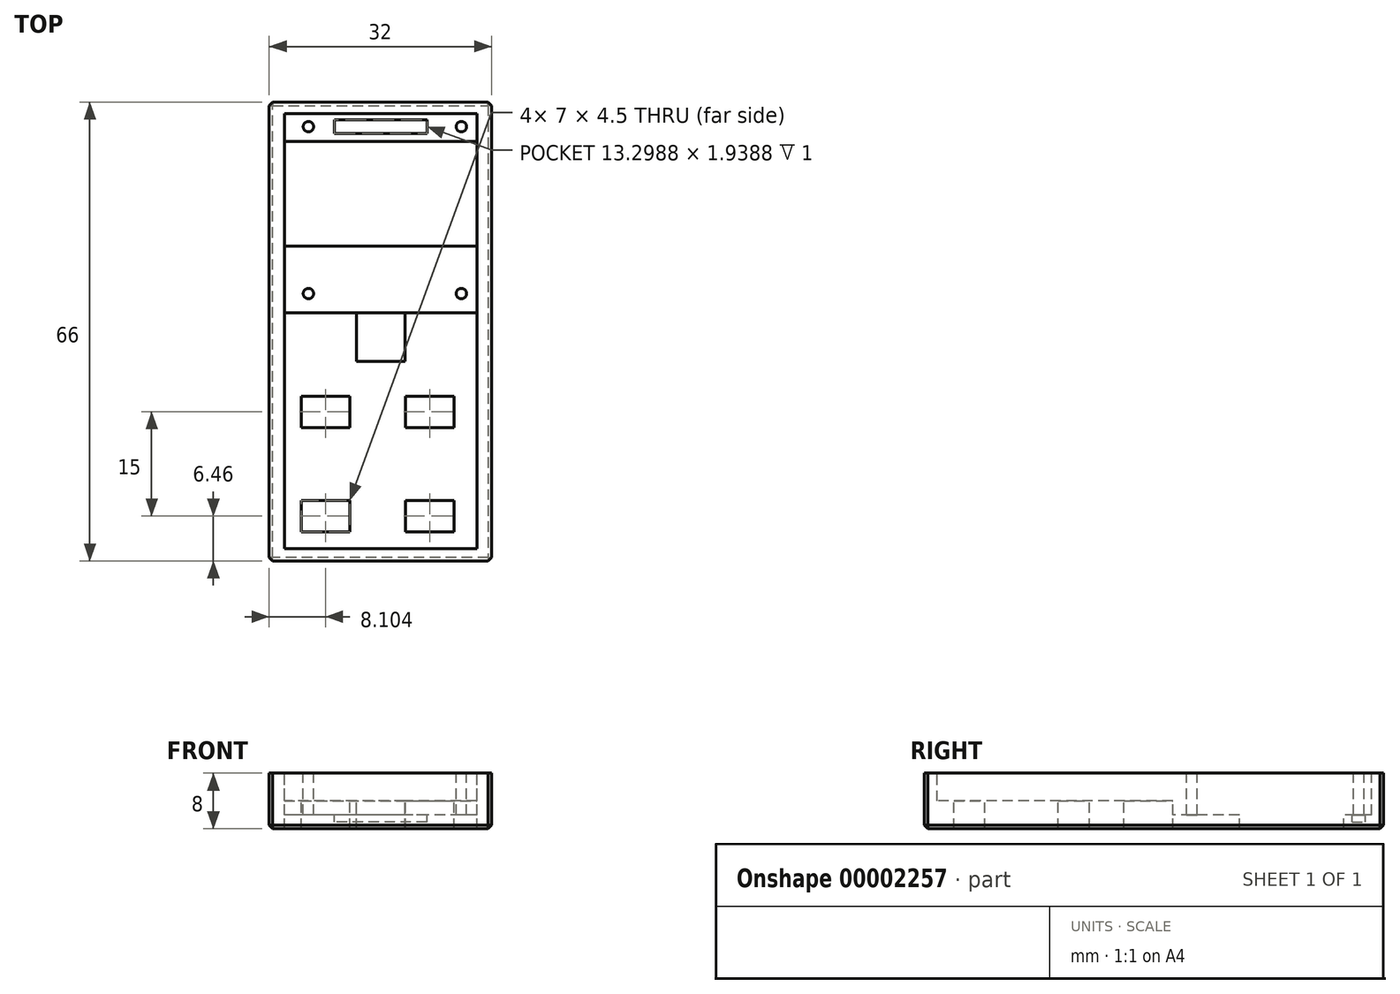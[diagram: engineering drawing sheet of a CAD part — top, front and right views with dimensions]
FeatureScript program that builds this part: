
annotation { "Feature Type Name" : "Feature", "Feature Type Description" : "" }
export const myFeature = defineFeature(function(context is Context, id is Id, definition is map)
    precondition{}
    {
        {
            var Q0;
            Q0=qCreatedBy(makeId("Top.planeOp"),FACE);
            var sketch = newSketch(context, id + "F0", { "sketchPlane" : qUnion([Q0])});
            skLineSegment(sketch, "E0.bottom", {"start": v(-16.74, 44.5) * mm, "end": v(15.26, 44.5) * mm});
            skLineSegment(sketch, "E0.top", {"start": v(-16.74, -21.5) * mm, "end": v(15.26, -21.5) * mm});
            skLineSegment(sketch, "E0.left", {"start": v(-16.74, 44.5) * mm, "end": v(-16.74, -21.5) * mm});
            skLineSegment(sketch, "E0.right", {"start": v(15.26, 44.5) * mm, "end": v(15.26, -21.5) * mm});
            skSolve(sketch);
        }
        {
            var Q0;
            Q0=makeQuery(id+"F0.imprint","IMPRINT",FACE,{"disambiguationData":[TD([[makeQuery(id+"F0.imprint","IMPRINT",EDGE,{"derivedFrom":sQuery(id+"F0.wireOp",EDGE,"E0.bottom")}),-1.0]])]});
            extrude(context, id + "F1", {"entities" : qUnion([Q0]), "depth" : 8 * mm});
        }
        {
            var Q0;
            Q0=makeQuery(id+"F1.opExtrude","CAP_FACE",FACE,{"disambiguationData":[OSD([sQuery(id+"F0.wireOp",EDGE,"E0.bottom"),sQuery(id+"F0.wireOp",EDGE,"E0.top"),sQuery(id+"F0.wireOp",EDGE,"E0.left"),sQuery(id+"F0.wireOp",EDGE,"E0.right")])],"isStart":false});
            var sketch = newSketch(context, id + "F2", { "sketchPlane" : qUnion([Q0])});
            skLineSegment(sketch, "E1.bottom", {"start": v(-14.54, 42.81) * mm, "end": v(13.16, 42.81) * mm});
            skLineSegment(sketch, "E1.top", {"start": v(-14.54, -19.69) * mm, "end": v(13.16, -19.69) * mm});
            skLineSegment(sketch, "E1.left", {"start": v(-14.54, 42.81) * mm, "end": v(-14.54, -19.69) * mm});
            skLineSegment(sketch, "E1.right", {"start": v(13.16, 42.81) * mm, "end": v(13.16, -19.69) * mm});
            skLineSegment(sketch, "E2.bottom", {"start": v(13.16, 38.81) * mm, "end": v(-14.54, 38.81) * mm});
            skLineSegment(sketch, "E2.top", {"start": v(13.16, 23.81) * mm, "end": v(-14.54, 23.81) * mm});
            skLineSegment(sketch, "E2.left", {"start": v(13.16, 38.81) * mm, "end": v(13.16, 23.81) * mm});
            skLineSegment(sketch, "E2.right", {"start": v(-14.54, 38.81) * mm, "end": v(-14.54, 23.81) * mm});
            skCircle(sketch, "E3", {"center": v(10.91, 40.96) * mm, "radius": 0.75 * mm});
            skCircle(sketch, "E4.1.0.0", {"center": v(-11.09, 40.96) * mm, "radius": 0.75 * mm});
            skLineSegment(sketch, "E4.direction1", {"start": v(10.91, 40.96) * mm, "end": v(-11.09, 40.96) * mm, "construction": true});
            skCircle(sketch, "E5.0.1.0", {"center": v(-11.09, 16.96) * mm, "radius": 0.75 * mm});
            skCircle(sketch, "E5.0.1.1", {"center": v(10.91, 16.96) * mm, "radius": 0.75 * mm});
            skLineSegment(sketch, "E5.direction1", {"start": v(-11.09, 40.96) * mm, "end": v(13.91, 40.96) * mm, "construction": true});
            skLineSegment(sketch, "E5.direction2", {"start": v(-11.09, 40.96) * mm, "end": v(-11.09, 16.96) * mm, "construction": true});
            skLineSegment(sketch, "E6.bottom", {"start": v(-12.14, -17.29) * mm, "end": v(-5.14, -17.29) * mm});
            skLineSegment(sketch, "E6.top", {"start": v(-12.14, -12.79) * mm, "end": v(-5.14, -12.79) * mm});
            skLineSegment(sketch, "E6.left", {"start": v(-12.14, -17.29) * mm, "end": v(-12.14, -12.79) * mm});
            skLineSegment(sketch, "E6.right", {"start": v(-5.14, -17.29) * mm, "end": v(-5.14, -12.79) * mm});
            skLineSegment(sketch, "E7.0.1.0", {"start": v(-12.14, 2.21) * mm, "end": v(-5.14, 2.21) * mm});
            skLineSegment(sketch, "E7.0.1.1", {"start": v(-12.14, -2.29) * mm, "end": v(-12.14, 2.21) * mm});
            skLineSegment(sketch, "E7.0.1.2", {"start": v(-12.14, -2.29) * mm, "end": v(-5.14, -2.29) * mm});
            skLineSegment(sketch, "E7.0.1.3", {"start": v(-5.14, -2.29) * mm, "end": v(-5.14, 2.21) * mm});
            skLineSegment(sketch, "E7.1.0.0", {"start": v(2.86, -12.79) * mm, "end": v(9.86, -12.79) * mm});
            skLineSegment(sketch, "E7.1.0.1", {"start": v(2.86, -17.29) * mm, "end": v(2.86, -12.79) * mm});
            skLineSegment(sketch, "E7.1.0.2", {"start": v(2.86, -17.29) * mm, "end": v(9.86, -17.29) * mm});
            skLineSegment(sketch, "E7.1.0.3", {"start": v(9.86, -17.29) * mm, "end": v(9.86, -12.79) * mm});
            skLineSegment(sketch, "E7.1.1.0", {"start": v(2.86, 2.21) * mm, "end": v(9.86, 2.21) * mm});
            skLineSegment(sketch, "E7.1.1.1", {"start": v(2.86, -2.29) * mm, "end": v(2.86, 2.21) * mm});
            skLineSegment(sketch, "E7.1.1.2", {"start": v(2.86, -2.29) * mm, "end": v(9.86, -2.29) * mm});
            skLineSegment(sketch, "E7.1.1.3", {"start": v(9.86, -2.29) * mm, "end": v(9.86, 2.21) * mm});
            skLineSegment(sketch, "E7.direction1", {"start": v(-12.7, -17.29) * mm, "end": v(2.3, -17.29) * mm, "construction": true});
            skLineSegment(sketch, "E7.direction2", {"start": v(-12.7, -17.29) * mm, "end": v(-12.7, -2.29) * mm, "construction": true});
            skLineSegment(sketch, "E8", {"start": v(-0.69, 42.81) * mm, "end": v(-0.69, 38.81) * mm, "construction": true});
            skLineSegment(sketch, "E9.bottom", {"start": v(5.96, 40) * mm, "end": v(-7.33, 40) * mm});
            skLineSegment(sketch, "E9.top", {"start": v(5.96, 41.93) * mm, "end": v(-7.33, 41.93) * mm});
            skLineSegment(sketch, "E9.left", {"start": v(5.96, 40) * mm, "end": v(5.96, 41.93) * mm});
            skLineSegment(sketch, "E9.right", {"start": v(-7.33, 40) * mm, "end": v(-7.33, 41.93) * mm});
            skPoint(sketch, "E9.middle", {"position": v(-0.69, 40.96) * mm});
            skPoint(sketch, "E9.middle.positionSnap0", {"position": v(-0.69, 40.81) * mm});
            skPoint(sketch, "E9.centerSnap0", {"position": v(-0.69, 40.81) * mm});
            skLineSegment(sketch, "E10", {"start": v(-0.69, 38.81) * mm, "end": v(-0.69, -19.69) * mm, "construction": true});
            skLineSegment(sketch, "E11.bottom", {"start": v(2.81, 7.21) * mm, "end": v(-4.19, 7.21) * mm});
            skLineSegment(sketch, "E11.top", {"start": v(2.81, 14.21) * mm, "end": v(-4.19, 14.21) * mm});
            skLineSegment(sketch, "E11.left", {"start": v(2.81, 7.21) * mm, "end": v(2.81, 14.21) * mm});
            skLineSegment(sketch, "E11.right", {"start": v(-4.19, 7.21) * mm, "end": v(-4.19, 14.21) * mm});
            skPoint(sketch, "E11.middle", {"position": v(-0.69, 11.9) * mm});
            skLineSegment(sketch, "E12.bottom", {"start": v(13.16, 14.21) * mm, "end": v(-14.54, 14.21) * mm});
            skLineSegment(sketch, "E12.top", {"start": v(13.16, 42.81) * mm, "end": v(-14.54, 42.81) * mm});
            skLineSegment(sketch, "E12.left", {"start": v(13.16, 14.21) * mm, "end": v(13.16, 42.81) * mm});
            skLineSegment(sketch, "E12.right", {"start": v(-14.54, 14.21) * mm, "end": v(-14.54, 42.81) * mm});
            skSolve(sketch);
        }
        {
            var Q0;
            Q0=makeQuery(id+"F2.imprint","IMPRINT",FACE,{"disambiguationData":[TD([[makeQuery(id+"F2.imprint","IMPRINT",EDGE,{"derivedFrom":sQuery(id+"F2.wireOp",EDGE,"E2.bottom")}),1.0]])]});
            var Q1;
            Q1=makeQuery(id+"F2.imprint","IMPRINT",FACE,{"disambiguationData":[TD([[makeQuery(id+"F2.imprint","IMPRINT",EDGE,{"derivedFrom":sQuery(id+"F2.wireOp",EDGE,"E7.1.1.0")}),-1.0]])]});
            var Q2;
            Q2=makeQuery(id+"F2.imprint","IMPRINT",FACE,{"disambiguationData":[TD([[makeQuery(id+"F2.imprint","IMPRINT",EDGE,{"derivedFrom":sQuery(id+"F2.wireOp",EDGE,"E7.0.1.0")}),-1.0]])]});
            var Q3;
            Q3=makeQuery(id+"F2.imprint","IMPRINT",FACE,{"disambiguationData":[TD([[makeQuery(id+"F2.imprint","IMPRINT",EDGE,{"derivedFrom":sQuery(id+"F2.wireOp",EDGE,"E6.bottom")}),1.0]])]});
            var Q4;
            Q4=makeQuery(id+"F2.imprint","IMPRINT",FACE,{"disambiguationData":[TD([[makeQuery(id+"F2.imprint","IMPRINT",EDGE,{"derivedFrom":sQuery(id+"F2.wireOp",EDGE,"E7.1.0.0")}),-1.0]])]});
            var Q5;
            Q5=makeQuery(id+"F2.imprint","IMPRINT",FACE,{"disambiguationData":[TD([[makeQuery(id+"F2.imprint","IMPRINT",EDGE,{"derivedFrom":sQuery(id+"F2.wireOp",EDGE,"E11.bottom")}),-1.0]])]});
            extrude(context, id + "F3", {"entities" : qUnion([Q0, Q1, Q2, Q3, Q4, Q5]), "operationType" : NewBodyOperationType.REMOVE, "endBound" : BoundingType.UP_TO_NEXT, "oppositeDirection" : true, "depth" : 25 * mm});
        }
        {
            var Q0;
            {var subQ2=sQuery(id+"F2.wireOp",EDGE,"E1.top");Q0=makeQuery(id+"F2.imprint","IMPRINT",FACE,{"disambiguationData":[TD([[makeQuery(id+"F2.imprint","IMPRINT",EDGE,{"derivedFrom":subQ2}),1.0]])]});}
            var Q1;
            {var subQ2=sQuery(id+"F2.wireOp",EDGE,"E1.bottom");Q1=makeQuery(id+"F2.imprint","IMPRINT",FACE,{"disambiguationData":[TD([[makeQuery(id+"F2.imprint","IMPRINT",EDGE,{"derivedFrom":subQ2}),-1.0]])]});}
            extrude(context, id + "F4", {"entities" : qUnion([Q0, Q1]), "operationType" : NewBodyOperationType.REMOVE, "oppositeDirection" : true, "depth" : 4 * mm});
        }
        {
            var Q0;
            Q0=makeQuery(id+"F3.boolean.opBoolean","COPY",EDGE,{"derivedFrom":makeQuery(id+"F3.opExtrude","CAP_EDGE",EDGE,{"disambiguationData":[OSD([sQuery(id+"F2.wireOp",EDGE,"E7.0.1.2")])],"isStart":false})});
            var Q1;
            Q1=makeQuery(id+"F3.boolean.opBoolean","COPY",EDGE,{"derivedFrom":makeQuery(id+"F3.opExtrude","CAP_EDGE",EDGE,{"disambiguationData":[OSD([sQuery(id+"F2.wireOp",EDGE,"E7.0.1.1")])],"isStart":false})});
            var Q2;
            Q2=makeQuery(id+"F3.boolean.opBoolean","COPY",EDGE,{"derivedFrom":makeQuery(id+"F3.opExtrude","CAP_EDGE",EDGE,{"disambiguationData":[OSD([sQuery(id+"F2.wireOp",EDGE,"E7.0.1.0")])],"isStart":false})});
            var Q3;
            Q3=makeQuery(id+"F3.boolean.opBoolean","COPY",EDGE,{"derivedFrom":makeQuery(id+"F3.opExtrude","CAP_EDGE",EDGE,{"disambiguationData":[OSD([sQuery(id+"F2.wireOp",EDGE,"E7.0.1.3")])],"isStart":false})});
            var Q4;
            Q4=makeQuery(id+"F3.boolean.opBoolean","COPY",EDGE,{"derivedFrom":makeQuery(id+"F3.opExtrude","CAP_EDGE",EDGE,{"disambiguationData":[OSD([sQuery(id+"F2.wireOp",EDGE,"E7.1.1.1")])],"isStart":false})});
            var Q5;
            Q5=makeQuery(id+"F3.boolean.opBoolean","COPY",EDGE,{"derivedFrom":makeQuery(id+"F3.opExtrude","CAP_EDGE",EDGE,{"disambiguationData":[OSD([sQuery(id+"F2.wireOp",EDGE,"E7.1.1.2")])],"isStart":false})});
            var Q6;
            Q6=makeQuery(id+"F3.boolean.opBoolean","COPY",EDGE,{"derivedFrom":makeQuery(id+"F3.opExtrude","CAP_EDGE",EDGE,{"disambiguationData":[OSD([sQuery(id+"F2.wireOp",EDGE,"E7.1.1.3")])],"isStart":false})});
            var Q7;
            Q7=makeQuery(id+"F3.boolean.opBoolean","COPY",EDGE,{"derivedFrom":makeQuery(id+"F3.opExtrude","CAP_EDGE",EDGE,{"disambiguationData":[OSD([sQuery(id+"F2.wireOp",EDGE,"E7.1.1.0")])],"isStart":false})});
            var Q8;
            Q8=makeQuery(id+"F3.boolean.opBoolean","COPY",EDGE,{"derivedFrom":makeQuery(id+"F3.opExtrude","CAP_EDGE",EDGE,{"disambiguationData":[OSD([sQuery(id+"F2.wireOp",EDGE,"E6.top")])],"isStart":false})});
            var Q9;
            Q9=makeQuery(id+"F3.boolean.opBoolean","COPY",EDGE,{"derivedFrom":makeQuery(id+"F3.opExtrude","CAP_EDGE",EDGE,{"disambiguationData":[OSD([sQuery(id+"F2.wireOp",EDGE,"E6.left")])],"isStart":false})});
            var Q10;
            Q10=makeQuery(id+"F3.boolean.opBoolean","COPY",EDGE,{"derivedFrom":makeQuery(id+"F3.opExtrude","CAP_EDGE",EDGE,{"disambiguationData":[OSD([sQuery(id+"F2.wireOp",EDGE,"E6.bottom")])],"isStart":false})});
            var Q11;
            Q11=makeQuery(id+"F3.boolean.opBoolean","COPY",EDGE,{"derivedFrom":makeQuery(id+"F3.opExtrude","CAP_EDGE",EDGE,{"disambiguationData":[OSD([sQuery(id+"F2.wireOp",EDGE,"E6.right")])],"isStart":false})});
            var Q12;
            Q12=makeQuery(id+"F3.boolean.opBoolean","COPY",EDGE,{"derivedFrom":makeQuery(id+"F3.opExtrude","CAP_EDGE",EDGE,{"disambiguationData":[OSD([sQuery(id+"F2.wireOp",EDGE,"E7.1.0.1")])],"isStart":false})});
            var Q13;
            Q13=makeQuery(id+"F3.boolean.opBoolean","COPY",EDGE,{"derivedFrom":makeQuery(id+"F3.opExtrude","CAP_EDGE",EDGE,{"disambiguationData":[OSD([sQuery(id+"F2.wireOp",EDGE,"E7.1.0.2")])],"isStart":false})});
            var Q14;
            Q14=makeQuery(id+"F3.boolean.opBoolean","COPY",EDGE,{"derivedFrom":makeQuery(id+"F3.opExtrude","CAP_EDGE",EDGE,{"disambiguationData":[OSD([sQuery(id+"F2.wireOp",EDGE,"E7.1.0.3")])],"isStart":false})});
            var Q15;
            Q15=makeQuery(id+"F3.boolean.opBoolean","COPY",EDGE,{"derivedFrom":makeQuery(id+"F3.opExtrude","CAP_EDGE",EDGE,{"disambiguationData":[OSD([sQuery(id+"F2.wireOp",EDGE,"E7.1.0.0")])],"isStart":false})});
            var Q16;
            Q16=makeQuery(id+"F3.boolean.opBoolean","COPY",EDGE,{"derivedFrom":makeQuery(id+"F3.opExtrude","CAP_EDGE",EDGE,{"disambiguationData":[OSD([sQuery(id+"F2.wireOp",EDGE,"E2.top")])],"isStart":false})});
            var Q17;
            Q17=makeQuery(id+"F3.boolean.opBoolean","COPY",EDGE,{"derivedFrom":makeQuery(id+"F3.opExtrude","TWEAK_EDGE",EDGE,{"derivedFrom":[makeQuery(id+"F1.opExtrude","CAP_FACE",FACE,{"disambiguationData":[OSD([sQuery(id+"F0.wireOp",EDGE,"E0.bottom"),sQuery(id+"F0.wireOp",EDGE,"E0.top"),sQuery(id+"F0.wireOp",EDGE,"E0.left"),sQuery(id+"F0.wireOp",EDGE,"E0.right")])],"isStart":true}),makeQuery(id+"F2.imprint","IMPRINT",EDGE,{"derivedFrom":sQuery(id+"F2.wireOp",EDGE,"E2.right")})]})});
            var Q18;
            Q18=makeQuery(id+"F3.boolean.opBoolean","COPY",EDGE,{"derivedFrom":makeQuery(id+"F3.opExtrude","CAP_EDGE",EDGE,{"disambiguationData":[OSD([sQuery(id+"F2.wireOp",EDGE,"E2.bottom")])],"isStart":false})});
            var Q19;
            Q19=makeQuery(id+"F3.boolean.opBoolean","COPY",EDGE,{"derivedFrom":makeQuery(id+"F3.opExtrude","TWEAK_EDGE",EDGE,{"derivedFrom":[makeQuery(id+"F1.opExtrude","CAP_FACE",FACE,{"disambiguationData":[OSD([sQuery(id+"F0.wireOp",EDGE,"E0.bottom"),sQuery(id+"F0.wireOp",EDGE,"E0.top"),sQuery(id+"F0.wireOp",EDGE,"E0.left"),sQuery(id+"F0.wireOp",EDGE,"E0.right")])],"isStart":true}),makeQuery(id+"F2.imprint","IMPRINT",EDGE,{"derivedFrom":sQuery(id+"F2.wireOp",EDGE,"E2.left")})]})});
            var Q20;
            Q20=makeQuery(id+"F1.opExtrude","CAP_EDGE",EDGE,{"disambiguationData":[OSD([sQuery(id+"F0.wireOp",EDGE,"E0.left")])],"isStart":true});
            var Q21;
            Q21=makeQuery(id+"F1.opExtrude","CAP_EDGE",EDGE,{"disambiguationData":[OSD([sQuery(id+"F0.wireOp",EDGE,"E0.bottom")])],"isStart":true});
            var Q22;
            Q22=makeQuery(id+"F1.opExtrude","CAP_EDGE",EDGE,{"disambiguationData":[OSD([sQuery(id+"F0.wireOp",EDGE,"E0.top")])],"isStart":true});
            var Q23;
            Q23=makeQuery(id+"F1.opExtrude","CAP_EDGE",EDGE,{"disambiguationData":[OSD([sQuery(id+"F0.wireOp",EDGE,"E0.right")])],"isStart":true});
            var Q24;
            Q24=makeQuery(id+"F4.boolean.opBoolean","COPY",EDGE,{"derivedFrom":makeQuery(id+"F4.opExtrude","CAP_EDGE",EDGE,{"disambiguationData":[OSD([sQuery(id+"F2.wireOp",EDGE,"E6.bottom")])],"isStart":false})});
            var Q25;
            Q25=makeQuery(id+"F4.boolean.opBoolean","COPY",EDGE,{"derivedFrom":makeQuery(id+"F4.opExtrude","CAP_EDGE",EDGE,{"disambiguationData":[OSD([sQuery(id+"F2.wireOp",EDGE,"E6.top")])],"isStart":false})});
            var Q26;
            Q26=makeQuery(id+"F4.boolean.opBoolean","COPY",EDGE,{"derivedFrom":makeQuery(id+"F4.opExtrude","CAP_EDGE",EDGE,{"disambiguationData":[OSD([sQuery(id+"F2.wireOp",EDGE,"E6.right")])],"isStart":false})});
            var Q27;
            Q27=makeQuery(id+"F4.boolean.opBoolean","COPY",EDGE,{"derivedFrom":makeQuery(id+"F4.opExtrude","CAP_EDGE",EDGE,{"disambiguationData":[OSD([sQuery(id+"F2.wireOp",EDGE,"E6.left")])],"isStart":false})});
            var Q28;
            Q28=makeQuery(id+"F4.boolean.opBoolean","COPY",EDGE,{"derivedFrom":makeQuery(id+"F4.opExtrude","CAP_EDGE",EDGE,{"disambiguationData":[OSD([sQuery(id+"F2.wireOp",EDGE,"E7.0.1.2")])],"isStart":false})});
            var Q29;
            Q29=makeQuery(id+"F4.boolean.opBoolean","COPY",EDGE,{"derivedFrom":makeQuery(id+"F4.opExtrude","CAP_EDGE",EDGE,{"disambiguationData":[OSD([sQuery(id+"F2.wireOp",EDGE,"E7.0.1.0")])],"isStart":false})});
            var Q30;
            Q30=makeQuery(id+"F4.boolean.opBoolean","COPY",EDGE,{"derivedFrom":makeQuery(id+"F4.opExtrude","CAP_EDGE",EDGE,{"disambiguationData":[OSD([sQuery(id+"F2.wireOp",EDGE,"E7.0.1.3")])],"isStart":false})});
            var Q31;
            Q31=makeQuery(id+"F4.boolean.opBoolean","COPY",EDGE,{"derivedFrom":makeQuery(id+"F4.opExtrude","CAP_EDGE",EDGE,{"disambiguationData":[OSD([sQuery(id+"F2.wireOp",EDGE,"E7.0.1.1")])],"isStart":false})});
            var Q32;
            Q32=makeQuery(id+"F4.boolean.opBoolean","COPY",EDGE,{"derivedFrom":makeQuery(id+"F4.opExtrude","CAP_EDGE",EDGE,{"disambiguationData":[OSD([sQuery(id+"F2.wireOp",EDGE,"E7.1.1.1")])],"isStart":false})});
            var Q33;
            Q33=makeQuery(id+"F4.boolean.opBoolean","COPY",EDGE,{"derivedFrom":makeQuery(id+"F4.opExtrude","CAP_EDGE",EDGE,{"disambiguationData":[OSD([sQuery(id+"F2.wireOp",EDGE,"E7.1.1.0")])],"isStart":false})});
            var Q34;
            Q34=makeQuery(id+"F4.boolean.opBoolean","COPY",EDGE,{"derivedFrom":makeQuery(id+"F4.opExtrude","CAP_EDGE",EDGE,{"disambiguationData":[OSD([sQuery(id+"F2.wireOp",EDGE,"E7.1.1.3")])],"isStart":false})});
            var Q35;
            Q35=makeQuery(id+"F4.boolean.opBoolean","COPY",EDGE,{"derivedFrom":makeQuery(id+"F4.opExtrude","CAP_EDGE",EDGE,{"disambiguationData":[OSD([sQuery(id+"F2.wireOp",EDGE,"E7.1.1.2")])],"isStart":false})});
            var Q36;
            Q36=makeQuery(id+"F4.boolean.opBoolean","COPY",EDGE,{"derivedFrom":makeQuery(id+"F4.opExtrude","CAP_EDGE",EDGE,{"disambiguationData":[OSD([sQuery(id+"F2.wireOp",EDGE,"E7.1.0.0")])],"isStart":false})});
            var Q37;
            Q37=makeQuery(id+"F4.boolean.opBoolean","COPY",EDGE,{"derivedFrom":makeQuery(id+"F4.opExtrude","CAP_EDGE",EDGE,{"disambiguationData":[OSD([sQuery(id+"F2.wireOp",EDGE,"E7.1.0.3")])],"isStart":false})});
            var Q38;
            Q38=makeQuery(id+"F4.boolean.opBoolean","COPY",EDGE,{"derivedFrom":makeQuery(id+"F4.opExtrude","CAP_EDGE",EDGE,{"disambiguationData":[OSD([sQuery(id+"F2.wireOp",EDGE,"E7.1.0.2")])],"isStart":false})});
            var Q39;
            Q39=makeQuery(id+"F4.boolean.opBoolean","COPY",EDGE,{"derivedFrom":makeQuery(id+"F4.opExtrude","CAP_EDGE",EDGE,{"disambiguationData":[OSD([sQuery(id+"F2.wireOp",EDGE,"E7.1.0.1")])],"isStart":false})});
            var Q40;
            Q40=makeQuery(id+"F4.boolean.opBoolean","COPY",EDGE,{"derivedFrom":makeQuery(id+"F4.opExtrude","CAP_EDGE",EDGE,{"disambiguationData":[OSD([sQuery(id+"F2.wireOp",EDGE,"E2.bottom")])],"isStart":false})});
            var Q41;
            Q41=makeQuery(id+"F4.boolean.opBoolean","COPY",EDGE,{"derivedFrom":makeQuery(id+"F4.opExtrude","CAP_EDGE",EDGE,{"disambiguationData":[OSD([sQuery(id+"F2.wireOp",EDGE,"E2.top")])],"isStart":false})});
            var Q42;
            Q42=makeQuery(id+"F4.boolean.opBoolean","COPY",EDGE,{"derivedFrom":makeQuery(id+"F4.opExtrude","CAP_EDGE",EDGE,{"disambiguationData":[OSD([sQuery(id+"F2.wireOp",EDGE,"E11.left")])],"isStart":false})});
            var Q43;
            Q43=makeQuery(id+"F4.boolean.opBoolean","COPY",EDGE,{"derivedFrom":makeQuery(id+"F4.opExtrude","CAP_EDGE",EDGE,{"disambiguationData":[OSD([sQuery(id+"F2.wireOp",EDGE,"E11.top")])],"isStart":false})});
            var Q44;
            Q44=makeQuery(id+"F4.boolean.opBoolean","COPY",EDGE,{"derivedFrom":makeQuery(id+"F4.opExtrude","CAP_EDGE",EDGE,{"disambiguationData":[OSD([sQuery(id+"F2.wireOp",EDGE,"E11.right")])],"isStart":false})});
            var Q45;
            Q45=makeQuery(id+"F4.boolean.opBoolean","COPY",EDGE,{"derivedFrom":makeQuery(id+"F4.opExtrude","CAP_EDGE",EDGE,{"disambiguationData":[OSD([sQuery(id+"F2.wireOp",EDGE,"E11.bottom")])],"isStart":false})});
            var Q46;
            Q46=makeQuery(id+"F3.boolean.opBoolean","COPY",EDGE,{"derivedFrom":makeQuery(id+"F3.opExtrude","TWEAK_EDGE",EDGE,{"derivedFrom":[makeQuery(id+"F1.opExtrude","CAP_FACE",FACE,{"disambiguationData":[OSD([sQuery(id+"F0.wireOp",EDGE,"E0.bottom"),sQuery(id+"F0.wireOp",EDGE,"E0.top"),sQuery(id+"F0.wireOp",EDGE,"E0.left"),sQuery(id+"F0.wireOp",EDGE,"E0.right")])],"isStart":true}),makeQuery(id+"F2.imprint","IMPRINT",EDGE,{"derivedFrom":sQuery(id+"F2.wireOp",EDGE,"E11.top")})]})});
            var Q47;
            Q47=makeQuery(id+"F3.boolean.opBoolean","COPY",EDGE,{"derivedFrom":makeQuery(id+"F3.opExtrude","CAP_EDGE",EDGE,{"disambiguationData":[OSD([sQuery(id+"F2.wireOp",EDGE,"E11.left")])],"isStart":false})});
            var Q48;
            Q48=makeQuery(id+"F3.boolean.opBoolean","COPY",EDGE,{"derivedFrom":makeQuery(id+"F3.opExtrude","CAP_EDGE",EDGE,{"disambiguationData":[OSD([sQuery(id+"F2.wireOp",EDGE,"E11.right")])],"isStart":false})});
            var Q49;
            Q49=makeQuery(id+"F3.boolean.opBoolean","COPY",EDGE,{"derivedFrom":makeQuery(id+"F3.opExtrude","CAP_EDGE",EDGE,{"disambiguationData":[OSD([sQuery(id+"F2.wireOp",EDGE,"E11.bottom")])],"isStart":false})});
            var Q50;
            Q50=makeQuery(id+"F1.opExtrude","SWEPT_EDGE",EDGE,{"disambiguationData":[OSD([sQuery(id+"F0.wireOp",EDGE,"E0.bottom"),sQuery(id+"F0.wireOp",EDGE,"E0.left")])]});
            var Q51;
            Q51=makeQuery(id+"F1.opExtrude","SWEPT_EDGE",EDGE,{"disambiguationData":[OSD([sQuery(id+"F0.wireOp",EDGE,"E0.bottom"),sQuery(id+"F0.wireOp",EDGE,"E0.right")])]});
            var Q52;
            Q52=makeQuery(id+"F1.opExtrude","SWEPT_EDGE",EDGE,{"disambiguationData":[OSD([sQuery(id+"F0.wireOp",EDGE,"E0.top"),sQuery(id+"F0.wireOp",EDGE,"E0.left")])]});
            var Q53;
            Q53=makeQuery(id+"F1.opExtrude","SWEPT_EDGE",EDGE,{"disambiguationData":[OSD([sQuery(id+"F0.wireOp",EDGE,"E0.top"),sQuery(id+"F0.wireOp",EDGE,"E0.right")])]});
            chamfer(context, id + "F5", {"entities" : qUnion([Q0, Q1, Q2, Q3, Q4, Q5, Q6, Q7, Q8, Q9, Q10, Q11, Q12, Q13, Q14, Q15, Q16, Q17, Q18, Q19, Q20, Q21, Q22, Q23, Q24, Q25, Q26, Q27, Q28, Q29, Q30, Q31, Q32, Q33, Q34, Q35, Q36, Q37, Q38, Q39, Q40, Q41, Q42, Q43, Q44, Q45, Q46, Q47, Q48, Q49, Q50, Q51, Q52, Q53]), "width" : .5 * mm, "tangentPropagation" : true});
        }
        {
            var Q0;
            Q0=makeQuery(id+"F2.imprint","IMPRINT",FACE,{"disambiguationData":[TD([[makeQuery(id+"F2.imprint","IMPRINT",EDGE,{"derivedFrom":sQuery(id+"F2.wireOp",EDGE,"E9.bottom")}),-1.0]])]});
            extrude(context, id + "F6", {"entities" : qUnion([Q0]), "operationType" : NewBodyOperationType.REMOVE, "oppositeDirection" : true, "depth" : 7 * mm});
        }
        {
            var Q0;
            {var subQ4=sQuery(id+"F2.wireOp",EDGE,"E2.top");Q0=makeQuery(id+"F2.imprint","IMPRINT",FACE,{"disambiguationData":[TD([[makeQuery(id+"F2.imprint","IMPRINT",EDGE,{"derivedFrom":subQ4}),1.0]])]});}
            var Q1;
            {var subQ0=sQuery(id+"F2.wireOp",EDGE,"E2.bottom");Q1=makeQuery(id+"F2.imprint","IMPRINT",FACE,{"disambiguationData":[TD([[makeQuery(id+"F2.imprint","IMPRINT",EDGE,{"derivedFrom":subQ0}),-1.0]])]});}
            extrude(context, id + "F7", {"entities" : qUnion([Q0, Q1]), "operationType" : NewBodyOperationType.REMOVE, "oppositeDirection" : true, "depth" : 6 * mm});
        }
    });
